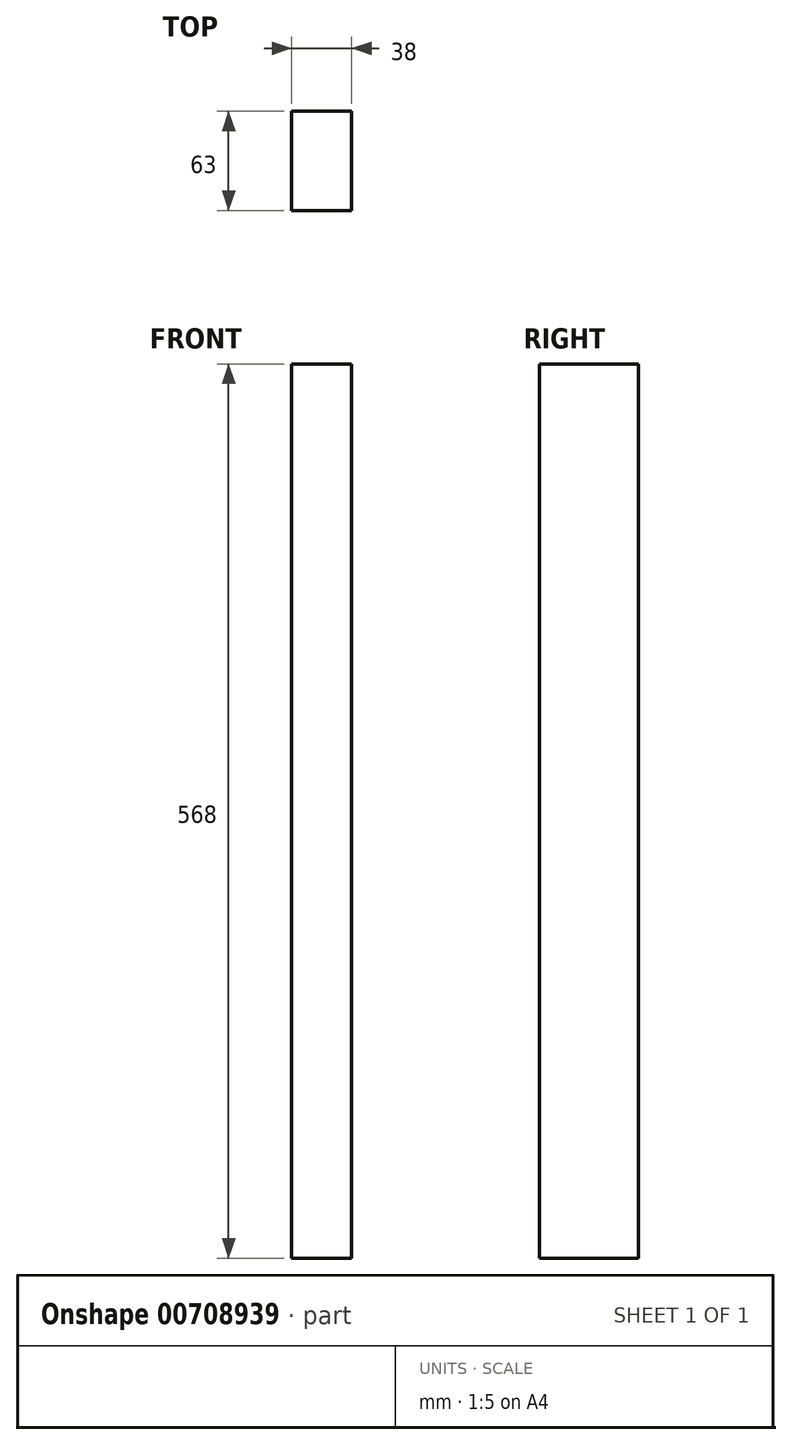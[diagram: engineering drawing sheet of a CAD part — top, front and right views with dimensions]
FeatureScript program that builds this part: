
annotation { "Feature Type Name" : "Feature", "Feature Type Description" : "" }
export const myFeature = defineFeature(function(context is Context, id is Id, definition is map)
    precondition{}
    {
        {
            var Q0;
            Q0=qCreatedBy(makeId("Top.planeOp"),FACE);
            var sketch = newSketch(context, id + "F0", { "sketchPlane" : qUnion([Q0])});
            skLineSegment(sketch, "E0.bottom", {"start": v(0, 0) * mm, "end": v(38, 0) * mm});
            skLineSegment(sketch, "E0.top", {"start": v(0, 63) * mm, "end": v(38, 63) * mm});
            skLineSegment(sketch, "E0.left", {"start": v(0, 0) * mm, "end": v(0, 63) * mm});
            skLineSegment(sketch, "E0.right", {"start": v(38, 0) * mm, "end": v(38, 63) * mm});
            skSolve(sketch);
        }
        {
            var Q0;
            Q0=makeQuery(id+"F0.imprint","IMPRINT",FACE,{"disambiguationData":[TD([[makeQuery(id+"F0.imprint","IMPRINT",EDGE,{"derivedFrom":sQuery(id+"F0.wireOp",EDGE,"E0.bottom")}),1.0]])]});
            extrude(context, id + "F1", {"entities" : qUnion([Q0]), "depth" : 568 * mm, "offsetDistance" : 25 * mm});
        }
    });
